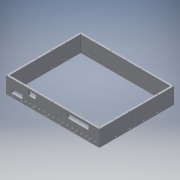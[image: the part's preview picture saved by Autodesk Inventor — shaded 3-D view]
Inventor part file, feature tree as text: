
AUTODESK INVENTOR PART (.ipt)
format: ipt  version: 2017 (Build 210142000, 142)  size: 584,192 bytes
history: native  units: in
note: dims shown in document units (in); Inventor stores cm internally (conversion verified against a paired STEP export)
features: hole x16, other x10, pattern_linear x10, fillet x8, extrude x4, projected_geometry x1, sketch x1
ambient origin geometry x8: Origin, YZ Plane, XZ Plane, XY Plane, X Axis, Y Axis, Z Axis, Center Point
bodies: Solid1 (feature_tree)
feature tree (50):
  extrude  "Extrusion1"  Depth=7.626in
  other  "left-2"
  other  "left-1"
  other  "bottom-1"
  hole  "Hole8"  [1 undecoded]
  hole  "Hole9"  [1 undecoded]
  other  "front-1"
  hole  "Hole10"  [1 undecoded]
  other  "right-1"
  hole  "Hole11"  [1 undecoded]
  hole  "Hole12"  [1 undecoded]
  pattern_linear  "Rectangular Pattern9"  Spacing1=0.0935in  [1 undecoded]
  pattern_linear  "Rectangular Pattern10"  Spacing1=0.0935in  [1 undecoded]
  pattern_linear  "Rectangular Pattern11"  Count1=6 Spacing1=1.562in
  pattern_linear  "Rectangular Pattern12"  Count1=7 Spacing1=1.635in
  hole  "Hole13"  [1 undecoded]
  hole  "Hole16"  [1 undecoded]
  hole  "Hole17"  [1 undecoded]
  extrude  "Extrusion2"  Depth=0.187in
  hole  "Hole18"  [1 undecoded]
  hole  "Hole19"  [1 undecoded]
  hole  "Hole20"  [1 undecoded]
  hole  "Hole21"  [1 undecoded]
  pattern_linear  "Rectangular Pattern13"  Spacing1=1.1693in  [1 undecoded]
  hole  "Hole22"  [1 undecoded]
  pattern_linear  "Rectangular Pattern14"  Spacing1=2.05in  [1 undecoded]
  pattern_linear  "Rectangular Pattern15"  Spacing1=0.41in  [1 undecoded]
  pattern_linear  "Rectangular Pattern16"  Spacing1=0.368in  [1 undecoded]
  pattern_linear  "Rectangular Pattern17"  Spacing1=1.0in  [1 undecoded]
  pattern_linear  "Rectangular Pattern19"  Spacing1=1.75in  [1 undecoded]
  fillet  "Fillet1"  Radius=0.185in
  fillet  "Fillet2"  Radius=1.0in
  fillet  "Fillet3"  Radius=0.185in
  fillet  "Fillet4"  Radius=0.185in
  fillet  "Fillet5"  Radius=1.75in
  fillet  "Fillet6"  Radius=0.185in
  fillet  "Fillet7"  Radius=0.3937in
  fillet  "Fillet8"  Radius=0.562in
  other  "dsub37"
  other  "dsub9"
  hole  "Hole_jackpost_dsub37"  [1 undecoded]
  extrude  "dsub37 cutout"  Depth=0.187in
  hole  "Hole_jackpost_dsub9"  [1 undecoded]
  extrude  "dsub9 cutout"  Depth=0.187in
  hole  "Hole26"  [1 undecoded]
  other  "Ext-Sketch"
  other  "back-1"
  other  "top"
  projected_geometry  "Projected Loop3"
  sketch  "Sketch30"  dims[d6=9.626in d8=7.626in d9=8.0in d10=10.0in d11=0.187in d12=0.187in d13=1.75in d14=0.0in d125=0.0935in d126=0.0935in d127=0.067in d128=0.2in d129=0.375in d130=0.25in d131=0.5635in d132=0.2in d133=0.8108in d134=2.3622in d136=1.562in d137=2.7559in d139=1.635in d140=0.0935in d141=0.0935in d142=0.067in d143=0.2in d144=0.375in d145=0.25in d146=0.5635in d147=0.2in d148=0.8108in d149=2.3622in d151=1.562in d152=2.7559in d154=1.635in d155=0.096in d156=0.75in d157=0.16in d158=0.25in d159=0.5635in d160=1.0in d161=0.8108in d162=0.096in d163=0.75in d164=0.16in d165=0.25in d166=0.5635in d167=1.0in d168=0.8108in d169=0.096in d170=0.75in d171=0.16in d172=0.25in d173=0.5635in d174=1.0in d175=0.8108in d176=0.095in d177=0.095in d180=0.067in d181=0.2in d182=0.375in d183=0.25in d184=0.5635in d185=0.2in d186=0.8108in d197=0.24in d203=0.48in d222=1.1693in d223=0.4094in d224=2.05in d225=0.41in d227=0.368in d238=0.067in d239=0.75in d240=0.375in d241=0.25in d242=0.5635in d243=1.0in d244=0.8108in d245=0.17in d246=0.75in d247=0.375in d248=0.25in d249=0.5635in d250=1.0in d251=0.8108in d252=1.0in d253=0.0in d254=1.75in d255=0.185in d256=1.0in d257=0.185in d259=0.185in d260=1.75in d261=0.185in d262=0.096in d263=0.75in d264=0.16in d265=0.25in d266=0.5635in d267=1.0in d268=0.8108in d271=6.2992in d273=0.5in d274=0.3937in d276=1.0in d278=0.17in d279=0.75in d280=0.375in d281=0.25in d282=0.5635in d283=1.0in d284=0.8108in d285=0.17in d286=0.75in d287=0.375in d288=0.25in d289=0.5635in d290=1.0in d291=0.8108in d292=0.067in d293=0.75in d294=0.375in d295=0.25in d296=0.5635in d297=0.2in d298=0.8108in d299=0.562in d300=2.05in d301=2.05in d302=0.65in d303=0.7874in d305=1.0in d306=0.25in d307=0.185in d308=0.096in d309=0.75in d310=0.16in d311=0.25in d312=0.5635in d313=1.0in d314=0.8108in d315=1.9685in d317=1.5in d318=2.3622in d320=1.6in d321=1.5748in d323=1.5in d324=1.5748in d326=1.5in d331=2.3622in d333=1.562in d334=2.7559in d336=1.635in d338=0.06in d339=0.06in d340=0.06in d341=0.06in d342=0.031in d343=0.031in d344=0.031in d345=0.031in d434=0.17in d477=2.3in d478=0.089in d479=0.089in d482=0.166in d483=0.166in d484=0.708in d485=0.583in d486=0.984in d490=0.23in d491=0.44in d492=0.166in d493=0.166in d496=0.089in d497=1.038in d498=0.089in d499=2.5in d500=0.264in d501=0.264in d502=0.264in d503=0.264in d504=1.983in d505=2.052in d506=0.132in d507=0.132in d508=0.132in d509=0.132in d510=0.21in d511=0.425in d515=0.085in d516=0.224in d517=0.375in d518=0.25in d519=0.5635in d520=0.187in d521=0.8108in d522=1.0in d523=0.0in d524=0.085in d525=0.224in d526=0.375in d527=0.25in d528=0.5635in d529=0.187in d530=0.8108in d531=1.0in d532=0.0in d537=0.085in d538=0.224in d539=0.375in d540=0.25in d541=0.5635in d542=0.187in d543=0.8108in d544=0.47in d545=0.47in d33=1.0in d34=1.0in d383=1.0in d384=1.0in]
note: 24 required parameter values undecoded (feature->parameter linkage not recoverable at this tier; creation-order binding heuristic only, values carry confidence <= 0.55)
